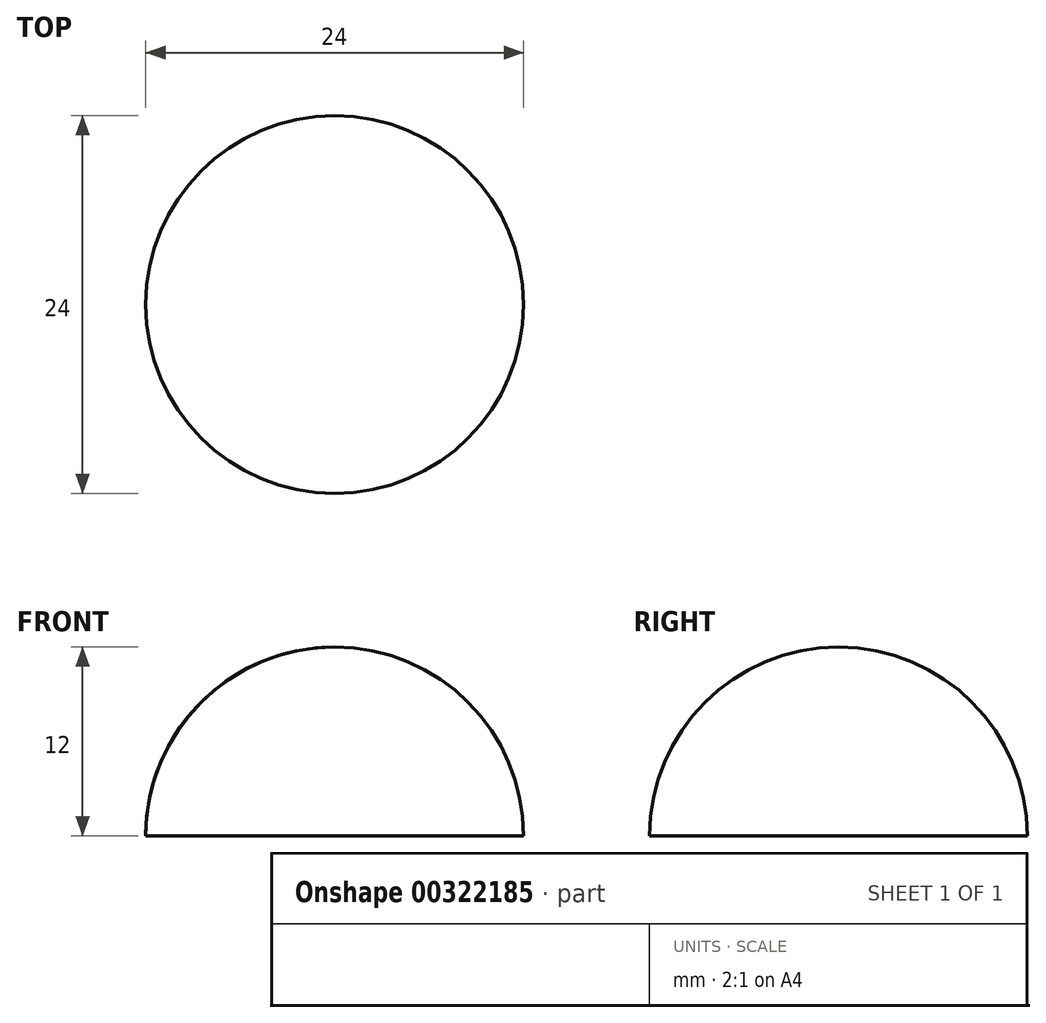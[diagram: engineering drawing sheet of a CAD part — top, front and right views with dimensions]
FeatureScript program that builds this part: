
annotation { "Feature Type Name" : "Feature", "Feature Type Description" : "" }
export const myFeature = defineFeature(function(context is Context, id is Id, definition is map)
    precondition{}
    {
        {
            var Q0;
            Q0=qCreatedBy(makeId("Front.planeOp"),FACE);
            var sketch = newSketch(context, id + "F0", { "sketchPlane" : qUnion([Q0])});
            skArc(sketch, "E0", {"start": v(0, 12) * mm, "mid": v(-8.49, 8.49) * mm, "end": v(-12, 0) * mm});
            skLineSegment(sketch, "E1", {"start": v(-12, 0) * mm, "end": v(0, 0) * mm});
            skLineSegment(sketch, "E2", {"start": v(0, 0) * mm, "end": v(0, 12) * mm});
            skSolve(sketch);
        }
        {
            var Q0;
            Q0=makeQuery(id+"F0.imprint","IMPRINT",FACE,{"disambiguationData":[TD([[makeQuery(id+"F0.imprint","IMPRINT",EDGE,{"derivedFrom":sQuery(id+"F0.wireOp",EDGE,"E0")}),1.0]])]});
            var Q1;
            Q1=sQuery(id+"F0.wireOp",EDGE,"E2");
            revolve(context, id + "F1", {"entities" : qUnion([Q0]), "axis" : qUnion([Q1]), "revolveType" : RevolveType.FULL});
        }
    });
